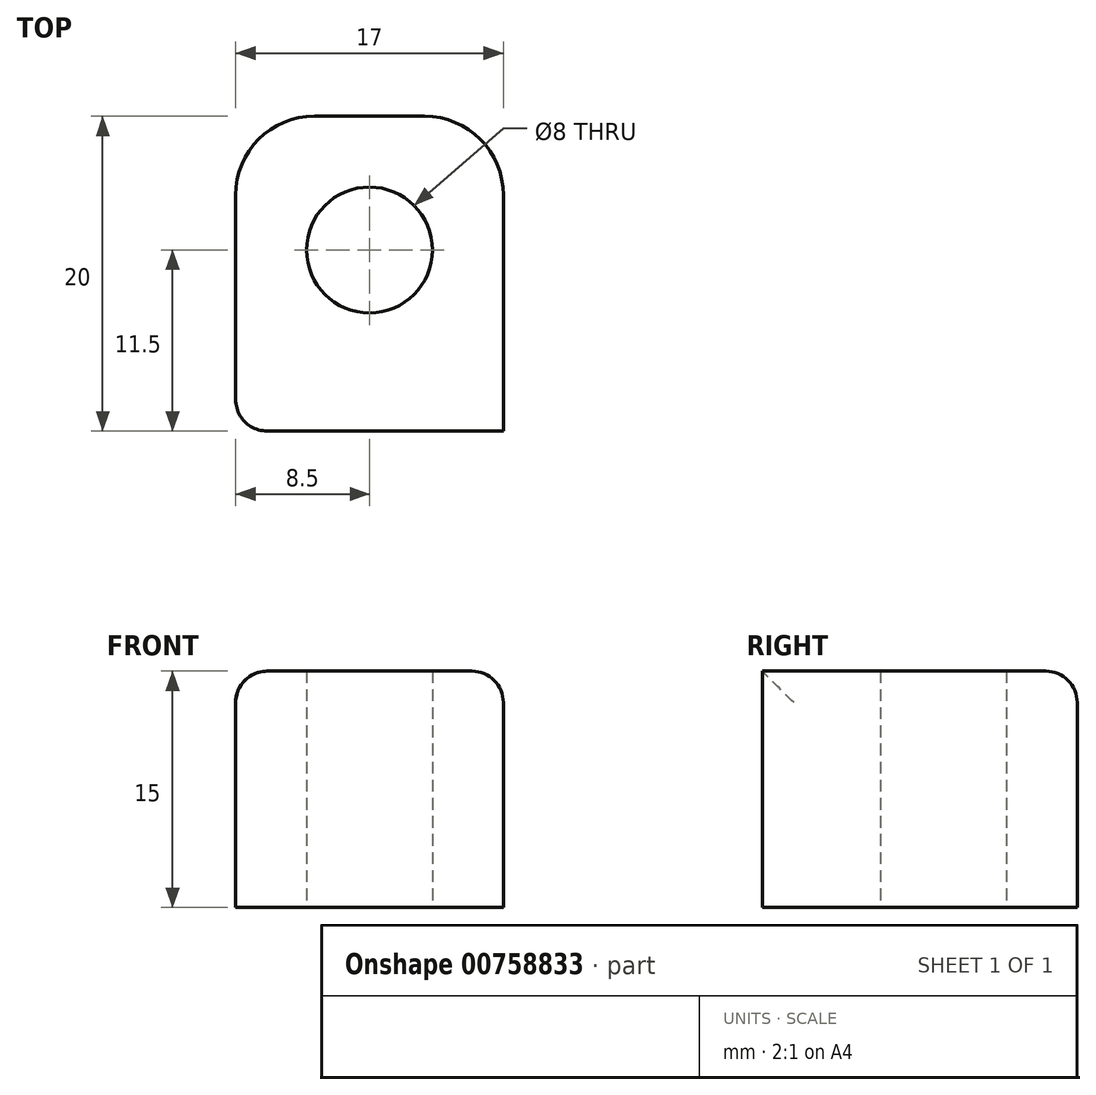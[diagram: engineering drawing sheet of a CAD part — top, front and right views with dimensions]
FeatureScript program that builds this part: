
annotation { "Feature Type Name" : "Feature", "Feature Type Description" : "" }
export const myFeature = defineFeature(function(context is Context, id is Id, definition is map)
    precondition{}
    {
        {
            var Q0;
            Q0=qCreatedBy(makeId("Top.planeOp"),FACE);
            var sketch = newSketch(context, id + "F0", { "sketchPlane" : qUnion([Q0])});
            skLineSegment(sketch, "E0.top", {"start": v(8.5, 15) * mm, "end": v(-8.5, 15) * mm});
            skLineSegment(sketch, "E0.left", {"start": v(8.5, -5) * mm, "end": v(8.5, 15) * mm});
            skLineSegment(sketch, "E0.right", {"start": v(-8.5, -5) * mm, "end": v(-8.5, 15) * mm});
            skCircle(sketch, "E1", {"center": v(0, 6.5) * mm, "radius": 4 * mm});
            skArc(sketch, "E2.0.startCap", {"start": v(-8.5, -25) * mm, "mid": v(-18.5, -15) * mm, "end": v(-8.5, -5) * mm});
            skArc(sketch, "E2.0.endCap", {"start": v(8.5, -5) * mm, "mid": v(18.5, -15) * mm, "end": v(8.5, -25) * mm});
            skLineSegment(sketch, "E2.0.left", {"start": v(-8.5, -5) * mm, "end": v(8.5, -5) * mm});
            skLineSegment(sketch, "E2.0.right", {"start": v(-8.5, -25) * mm, "end": v(8.5, -25) * mm});
            skArc(sketch, "E3.0", {"start": v(-8.5, -21) * mm, "mid": v(-14.5, -15) * mm, "end": v(-8.5, -9) * mm});
            skLineSegment(sketch, "E3.1", {"start": v(-8.5, -21) * mm, "end": v(8.5, -21) * mm});
            skArc(sketch, "E3.2", {"start": v(8.5, -9) * mm, "mid": v(14.5, -15) * mm, "end": v(8.5, -21) * mm});
            skLineSegment(sketch, "E4", {"start": v(-8.5, -9) * mm, "end": v(8.5, -9) * mm});
            skSolve(sketch);
        }
        {
            var Q0;
            Q0=makeQuery(id+"F0.imprint","IMPRINT",FACE,{"disambiguationData":[TD([[makeQuery(id+"F0.imprint","IMPRINT",EDGE,{"derivedFrom":sQuery(id+"F0.wireOp",EDGE,"E0.top")}),1.0]])]});
            var Q1;
            Q1=makeQuery(id+"F0.imprint","IMPRINT",FACE,{"disambiguationData":[TD([[makeQuery(id+"F0.imprint","IMPRINT",EDGE,{"derivedFrom":sQuery(id+"F0.wireOp",EDGE,"E2.0.startCap")}),-1.0]])]});
            extrude(context, id + "F1", {"entities" : qUnion([Q0, Q1]), "depth" : 15 * mm, "offsetDistance" : 25 * mm});
        }
        {
            var Q0;
            Q0=makeQuery(id+"F1.opExtrude","SWEPT_EDGE",EDGE,{"disambiguationData":[OSD([sQuery(id+"F0.wireOp",EDGE,"E0.top"),sQuery(id+"F0.wireOp",EDGE,"E0.right")])]});
            var Q1;
            Q1=makeQuery(id+"F1.opExtrude","SWEPT_EDGE",EDGE,{"disambiguationData":[OSD([sQuery(id+"F0.wireOp",EDGE,"E0.top"),sQuery(id+"F0.wireOp",EDGE,"E0.left")])]});
            fillet(context, id + "F2", {"entities" : qUnion([Q0, Q1]), "radius" : 5 * mm, "tangentPropagation" : true, "allowEdgeOverflow" : false});
        }
        {
            var Q0;
            Q0=makeQuery(id+"F1.opExtrude","SWEPT_FACE",FACE,{"disambiguationData":[OSD([sQuery(id+"F0.wireOp",EDGE,"E4")])]});
            var Q1;
            Q1=makeQuery(id+"F1.opExtrude","CAP_EDGE",EDGE,{"disambiguationData":[OSD([sQuery(id+"F0.wireOp",EDGE,"E2.0.endCap")])],"isStart":false});
            var Q2;
            Q2=makeQuery(id+"F1.opExtrude","CAP_EDGE",EDGE,{"disambiguationData":[OSD([sQuery(id+"F0.wireOp",EDGE,"E0.left")])],"isStart":false});
            var Q3;
            Q3=makeQuery(id+"F1.opExtrude","SWEPT_FACE",FACE,{"disambiguationData":[OSD([sQuery(id+"F0.wireOp",EDGE,"E2.0.endCap")])]});
            var Q4;
            Q4=makeQuery(id+"F1.opExtrude","CAP_EDGE",EDGE,{"disambiguationData":[OSD([sQuery(id+"F0.wireOp",EDGE,"E0.top")])],"isStart":false});
            var Q5;
            Q5=makeQuery(id+"F1.opExtrude","SWEPT_EDGE",EDGE,{"disambiguationData":[OSD([sQuery(id+"F0.wireOp",EDGE,"E0.right"),sQuery(id+"F0.wireOp",EDGE,"E2.0.startCap"),sQuery(id+"F0.wireOp",EDGE,"E2.0.left")])]});
            fillet(context, id + "F3", {"entities" : qUnion([Q0, Q1, Q2, Q3, Q4, Q5]), "radius" : 2 * mm, "tangentPropagation" : true, "allowEdgeOverflow" : false});
        }
    });
